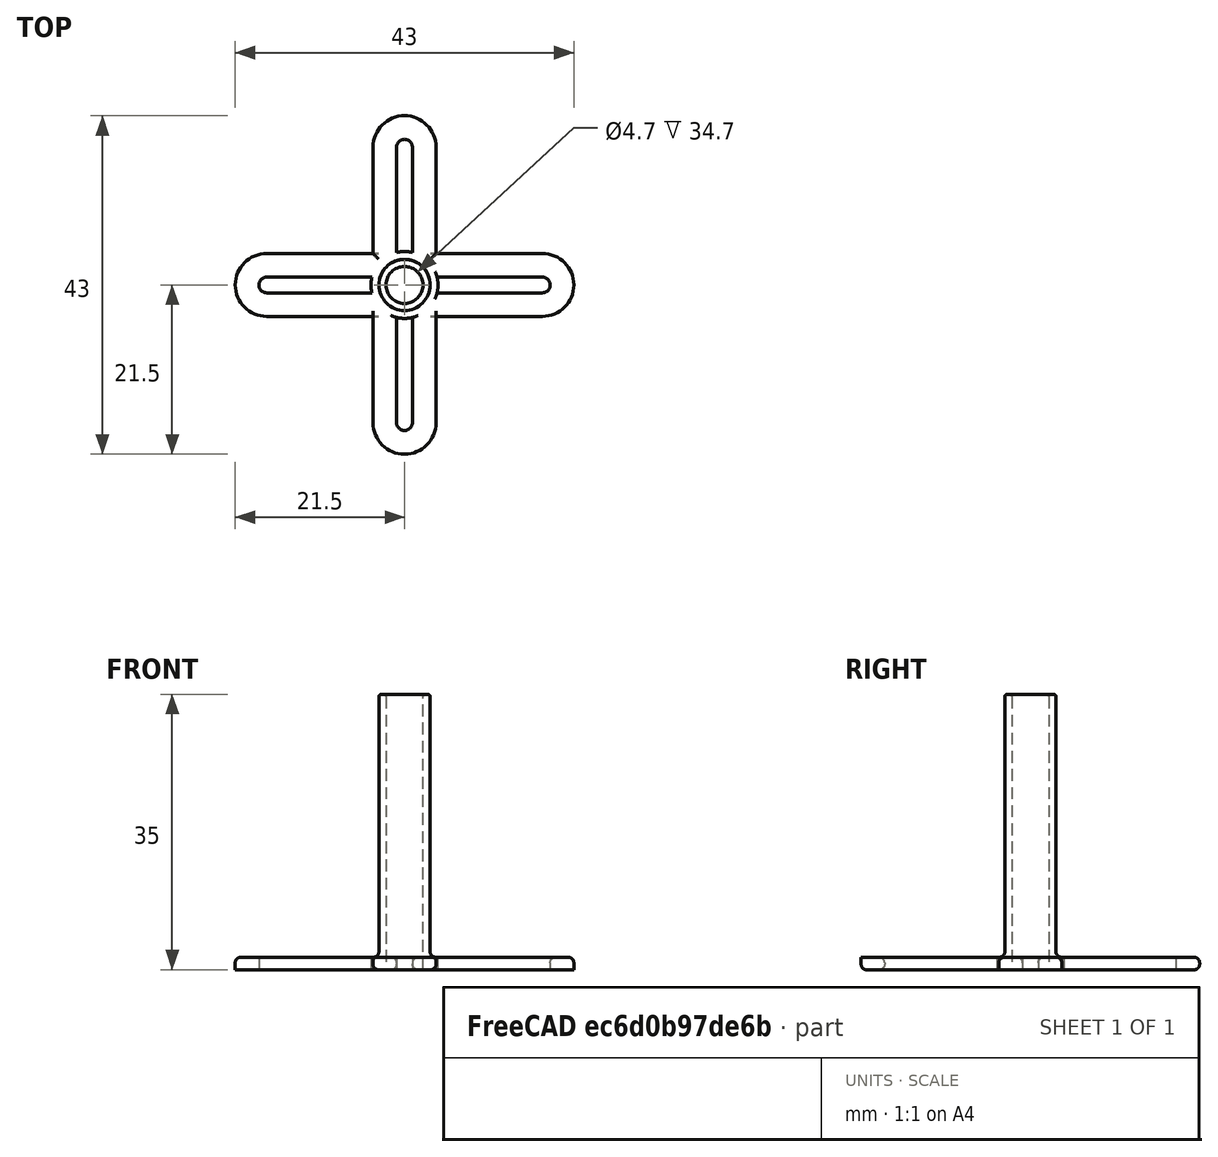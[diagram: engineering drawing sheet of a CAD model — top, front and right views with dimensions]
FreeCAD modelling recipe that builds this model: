
FCSTD DOCUMENT  (FreeCAD 0.20R29603 (Git))
Label: guia90grados
License: All rights reserved
LicenseURL: http://en.wikipedia.org/wiki/All_rights_reserved
objects: Part::Cylinder×7, Part::Cut×5, Part::Fillet×4, Part::MultiFuse×3, Sketcher::SketchObject×1, PartDesign::Pad×1, PartDesign::Body×1, Mesh::Feature×1
note: 23 computed .brp shape members not serialized (recipe doc carries the construction recipe); baked Part::Feature solids carry a one-line shape summary decoded from their .brp

FEATURE [Sketcher::SketchObject] Sketch
  FullyConstrained = false
  MapMode = 5
  Support = -> [XY_Plane]
  sketch-geometry (24):
    g0: ArcOfCircle CenterX=-17.5 CenterY=0 CenterZ=0 NormalX=0 NormalY=0 NormalZ=1 AngleXU=0 Radius=4 StartAngle=1.5708 EndAngle=4.71239
    g1: ArcOfCircle CenterX=17.5 CenterY=2e-16 CenterZ=0 NormalX=0 NormalY=0 NormalZ=1 AngleXU=0 Radius=4 StartAngle=4.71239 EndAngle=7.85398
    g2: LineSegment StartX=-17.5 StartY=-4 StartZ=0 EndX=-4 EndY=-4 EndZ=0
    g3: LineSegment StartX=17.5 StartY=4 StartZ=0 EndX=4 EndY=4 EndZ=0
    g4: ArcOfCircle CenterX=-17.5 CenterY=0 CenterZ=0 NormalX=0 NormalY=0 NormalZ=1 AngleXU=0 Radius=1 StartAngle=1.5708 EndAngle=4.71239
    g5: ArcOfCircle CenterX=17.5 CenterY=-1e-16 CenterZ=0 NormalX=0 NormalY=0 NormalZ=1 AngleXU=0 Radius=1 StartAngle=4.71239 EndAngle=7.85398
    g6: LineSegment StartX=-17.5 StartY=-1 StartZ=0 EndX=-1 EndY=-1 EndZ=0
    g7: LineSegment StartX=17.5 StartY=1 StartZ=0 EndX=1 EndY=1 EndZ=0
    g8: ArcOfCircle CenterX=6.22161e-11 CenterY=17.5 CenterZ=0 NormalX=0 NormalY=0 NormalZ=1 AngleXU=0 Radius=4 StartAngle=-1.7053e-12 EndAngle=3.14159
    g9: ArcOfCircle CenterX=-3.202e-13 CenterY=-17.5 CenterZ=0 NormalX=0 NormalY=0 NormalZ=1 AngleXU=0 Radius=4 StartAngle=3.14159 EndAngle=6.28319
    g10: LineSegment StartX=-4 StartY=17.5 StartZ=0 EndX=-4 EndY=4 EndZ=0
    g11: LineSegment StartX=4 StartY=-17.5 StartZ=0 EndX=4 EndY=-4 EndZ=0
    g12: ArcOfCircle CenterX=-6.8e-15 CenterY=17.5 CenterZ=0 NormalX=0 NormalY=0 NormalZ=1 AngleXU=0 Radius=1 StartAngle=-9e-16 EndAngle=3.14159
    g13: ArcOfCircle CenterX=-7e-15 CenterY=-17.5 CenterZ=0 NormalX=0 NormalY=0 NormalZ=1 AngleXU=0 Radius=1 StartAngle=3.14159 EndAngle=6.28319
    g14: LineSegment StartX=-1 StartY=17.5 StartZ=0 EndX=-1 EndY=1 EndZ=0
    g15: LineSegment StartX=1 StartY=-17.5 StartZ=0 EndX=1 EndY=-1 EndZ=0
    g16: LineSegment StartX=-1 StartY=1 StartZ=0 EndX=-17.5 EndY=1 EndZ=0
    g17: LineSegment StartX=-1 StartY=-1 StartZ=0 EndX=-1 EndY=-17.5 EndZ=0
    g18: LineSegment StartX=1 StartY=-1 StartZ=0 EndX=17.5 EndY=-1 EndZ=0
    g19: LineSegment StartX=1 StartY=1 StartZ=0 EndX=1 EndY=17.5 EndZ=0
    g20: LineSegment StartX=-4 StartY=4 StartZ=0 EndX=-17.5 EndY=4 EndZ=0
    g21: LineSegment StartX=4 StartY=4 StartZ=0 EndX=4 EndY=17.5 EndZ=0
    g22: LineSegment StartX=4 StartY=-4 StartZ=0 EndX=17.5 EndY=-4 EndZ=0
    g23: LineSegment StartX=-4 StartY=-4 StartZ=0 EndX=-4 EndY=-17.5 EndZ=0
  constraints (59):
    c: Tangent(g0,g2) = -1.5708
    c: Coincident(g22,g1) = -1.5708
    c: Tangent(g1,g3) = -1.5708
    c: Coincident(g20,g0) = -1.5708
    c: Equal(g0,g1)
    c: Horizontal(g3)
    c: Symmetric(g0,g1,g-1)
    c: DistanceY(g0,g0) = 8
    c: DistanceX(g0,g1) = 35
    c: Tangent(g4,g6) = -1.5708
    c: Coincident(g18,g5) = -1.5708
    c: Tangent(g5,g7) = -1.5708
    c: Coincident(g16,g4) = -1.5708
    c: Equal(g4,g5)
    c: Horizontal(g6)
    c: Symmetric(g4,g5,g-1)
    c: DistanceY(g4,g4) = 2
    c: DistanceX(g16,g7) = 35
    c: Tangent(g8,g10) = -1.5708
    c: Coincident(g23,g9) = -1.5708
    c: Tangent(g9,g11) = -1.5708
    c: Coincident(g21,g8) = -1.5708
    c: Equal(g8,g9)
    c: Vertical(g10)
    c: DistanceX(g8,g8) = 8
    c: Symmetric(g8,g9,g-1)
    c: Tangent(g12,g14) = -1.5708
    c: Coincident(g17,g13) = -1.5708
    c: Tangent(g13,g15) = -1.5708
    c: Coincident(g19,g12) = -1.5708
    c: Equal(g12,g13)
    c: Vertical(g14)
    c: Symmetric(g12,g13,g-1)
    c: DistanceX(g12,g12) = 2
    c: Coincident(g14,g16)
    c: Coincident(g6,g17)
    c: Coincident(g15,g18)
    c: Coincident(g19,g7)
    c: Coincident(g21,g3)
    c: Coincident(g22,g11)
    c: Coincident(g10,g20)
    c: Coincident(g2,g23)
    c: Equal(g2,g23)
    c: DistanceX(g2,g2) = 13.5
    c: Equal(g23,g11)
    c: Equal(g11,g22)
    c: Equal(g22,g3)
    c: Equal(g3,g21)
    c: Equal(g21,g10)
    c: Equal(g10,g20)
    c: Equal(g16,g6)
    c: Equal(g6,g17)
    c: Equal(g17,g15)
    c: Equal(g15,g18)
    c: Equal(g18,g7)
    c: Equal(g7,g19)
    c: Equal(g19,g14)
    c: DistanceX(g6,g6) = 16.5
    c: Horizontal(g16)
FEATURE [PartDesign::Pad] Pad
  Direction = (0,0,1)
  Length = 1.6
  Length2 = 10
  Profile = -> Sketch
  ReferenceAxis = -> Sketch [N_Axis]
  Type = 0
FEATURE [PartDesign::Body] Body
  Group = -> [Sketch,Pad]
  Origin = -> Origin
  Tip = -> Pad
FEATURE [Part::Cylinder] Cylinder
  Angle = 360
  AttacherType = Attacher::AttachEngine3D
  FirstAngle = 0
  Height = 35
  Radius = 3.25
  SecondAngle = 0
FEATURE [Part::Cylinder] Cylinder001
  Angle = 360
  AttacherType = Attacher::AttachEngine3D
  FirstAngle = 0
  Height = 35
  Radius = 2.35
  SecondAngle = 0
FEATURE [Part::Cut] Cut
  Base = -> Cylinder
  Tool = -> Cylinder001
FEATURE [Part::Cylinder] Cylinder002
  Angle = 360
  AttacherType = Attacher::AttachEngine3D
  FirstAngle = 0
  Height = 35
  Radius = 3
  SecondAngle = 0
FEATURE [Part::Cut] Cut001
  Base = -> Body
  Tool = -> Cylinder002
FEATURE [Part::MultiFuse] Fusion
  Shapes = -> [Cut,Cut001]
FEATURE [Part::Cylinder] Cylinder003
  Angle = 360
  AttacherType = Attacher::AttachEngine3D
  FirstAngle = 0
  Height = 1.6
  Radius = 4.25
  SecondAngle = 0
FEATURE [Part::Cylinder] Cylinder004
  Angle = 360
  AttacherType = Attacher::AttachEngine3D
  FirstAngle = 0
  Height = 35
  Radius = 2.35
  SecondAngle = 0
FEATURE [Part::Cut] Cut002
  Base = -> Cylinder003
  Tool = -> Cylinder004
FEATURE [Part::MultiFuse] Fusion001
  Shapes = -> [Cylinder003,Cylinder004,Cut002]
FEATURE [Part::MultiFuse] Fusion002
  Shapes = -> [Fusion,Fusion001]
FEATURE [Part::Fillet] Fillet
  Base = -> Fusion002
  Edges = 9 edges r=0.7: [Edge67,Edge68,Edge115,Edge118,Edge121,Edge123,Edge125,Edge126,Edge127]
FEATURE [Part::Fillet] Fillet001
  Base = -> Fillet
  Edges = 6 edges r=0.73: [Edge14,Edge19,Edge77,Edge78,Edge108,Edge117]
FEATURE [Part::Cylinder] Cylinder005
  Angle = 360
  AttacherType = Attacher::AttachEngine3D
  FirstAngle = 0
  Height = 35
  Radius = 2.35
  SecondAngle = 0
FEATURE [Part::Cut] Cut003
  Base = -> Fillet001
  Tool = -> Cylinder005
FEATURE [Part::Cylinder] Cylinder006
  Angle = 360
  AttacherType = Attacher::AttachEngine3D
  FirstAngle = 0
  Height = 35
  Radius = 2.35
  SecondAngle = 0
FEATURE [Part::Cut] Cut004
  Base = -> Cut003
  Tool = -> Cylinder006
FEATURE [Part::Fillet] Fillet002
  Base = -> Cut004
  Edges = 2 edges r=0.3: [Edge116,Edge186]
FEATURE [Part::Fillet] Fillet003
  Base = -> Fillet002
  Edges = 9 edges r=0.7: [Edge2,Edge3,Edge4,Edge5,Edge6,Edge7,Edge8,Edge9,Edge10]
FEATURE [Mesh::Feature] Mesh  label="Fillet003 (Meshed)"
